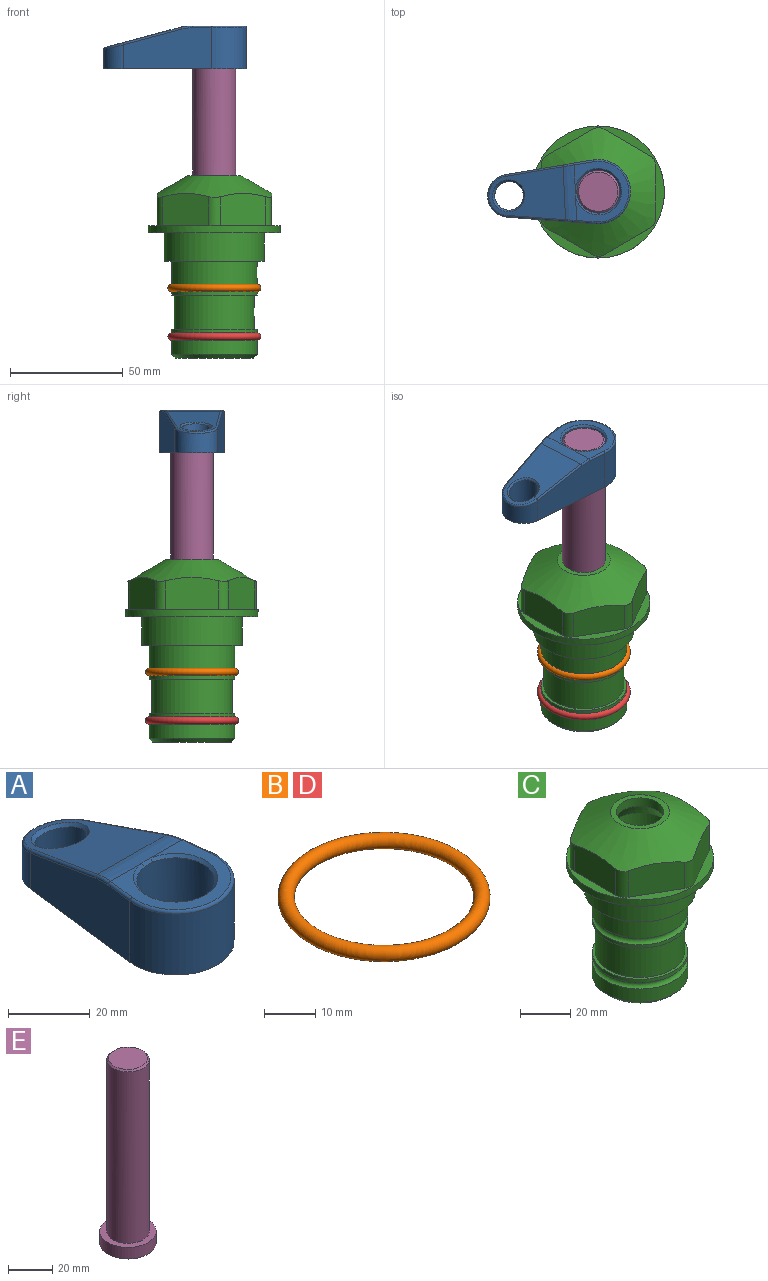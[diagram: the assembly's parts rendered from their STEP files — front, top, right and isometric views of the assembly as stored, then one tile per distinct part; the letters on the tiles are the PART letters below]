
ASSEMBLY  parts=5 mates=4
PART A: 31 faces, bbox 31.7x65.5x19.8 mm
  f0: plane 39.12x18.26mm, normal (0.99,0.12,0), area 612.2mm2, adj f1,f4,f7,f11,f13,f15
  f1: cylinder r=9.53mm len=18.91mm, axis (0,0,-1), area 296.1mm2, adj f0,f2,f7,f17
  f2: plane 39.12x18.26mm, normal (-0.99,0.12,0), area 612.2mm2, adj f1,f4,f7,f12,f14,f16
  f3: cylinder r=6.35mm len=12.7mm, axis (0,0,-1), area 362.4mm2, adj f7,f18
  f4: cylinder r=14.29mm len=28.58mm, axis (0,0,-1), area 882.2mm2, adj f0,f2,f7,f10
  f5: cylinder r=9.53mm len=19.05mm, axis (0,0,-1), area 1092.6mm2, adj f7,f19,f20
  f6: plane 26.99x23.69mm, normal (0,0,1), area 216.2mm2, adj f9,f10,f11,f12,f19
  f7: plane 63.5x28.58mm, normal (0,0,-1), area 661.8mm2, adj f0,f1,f2,f3,f4,f5,f22,f23
  f8: plane 33.52x23.6mm, normal (0,0.26,0.97), area 486mm2, adj f9,f15,f16,f17,f18
  f9: cylinder r=19.05mm len=24.72mm, axis (1,0,0), area 120.4mm2, adj f6,f8,f13,f14,f20
  f10: torus R=13.49mm, axis (0,0,1), area 59mm2, adj f4,f6,f11,f12
  f11: cylinder r=0.79mm len=8.67mm, axis (0.12,-0.99,0), area 10.8mm2, adj f0,f6,f10,f13
  f12: cylinder r=0.79mm len=8.67mm, axis (0.12,0.99,0), area 10.8mm2, adj f2,f6,f10,f14
  f13: bspline ~4.95x1.42mm, area 6.1mm2, adj f0,f9,f11,f15
  f14: bspline ~4.95x1.42mm, area 6.1mm2, adj f2,f9,f12,f16
  f15: cylinder r=0.79mm len=25.95mm, axis (0.12,-0.96,0.26), area 32.9mm2, adj f0,f8,f13,f17
  f16: cylinder r=0.79mm len=25.95mm, axis (0.12,0.96,-0.26), area 32.9mm2, adj f2,f8,f14,f17
  f17: bspline ~18.91x8.38mm, area 30mm2, adj f1,f8,f15,f16
  f18: bspline ~14.29x14.29mm, area 48.3mm2, adj f3,f8
  f19: cone r=9.53mm half-angle=45deg, axis (0,0,1), area 66.5mm2, adj f5,f6,f20
  f20: bspline ~3.22x0.96mm, area 3.5mm2, adj f5,f9,f19
  f21: plane 2.75x2.72mm, normal (0,0,-1), area 2.9mm2, adj f23,f25,f28
  f22: plane 23.05x15.88mm, normal (-0.99,-0.12,0), area 323.6mm2, adj f7,f25,f26,f27,f28,f29
  f23: plane 23.05x15.88mm, normal (0.99,-0.12,0), area 323.6mm2, adj f7,f21,f25,f27,f28,f30
  f24: cylinder r=9.53mm len=10.69mm, axis (0,0,-1), area 114.7mm2, adj f7,f27,f29,f30
  f25: cylinder r=12.7mm len=20.59mm, axis (0,0,-1), area 381.1mm2, adj f7,f21,f22,f23,f26,f28
  f26: plane 2.75x2.72mm, normal (0,0,-1), area 2.9mm2, adj f22,f25,f28
  f27: plane 19.72x18.37mm, normal (0,-0.26,-0.97), area 291.8mm2, adj f22,f23,f24,f28,f29,f30
  f28: cylinder r=15.88mm len=19.92mm, axis (1,0,0), area 54.8mm2, adj f21,f22,f23,f25,f26,f27
  f29: cylinder r=1.59mm len=11mm, axis (0,0,-1), area 34.7mm2, adj f7,f22,f24,f27
  f30: cylinder r=1.59mm len=11mm, axis (0,0,-1), area 34.7mm2, adj f7,f23,f24,f27
PART B: 1 faces, bbox 44.7x44.7x3.2 mm
  f0: torus R=19.05mm, axis (0,0,1), area 1193.9mm2
PART C: 36 faces, bbox 58.7x58.7x81 mm
  f0: cylinder r=17.78mm len=35.56mm, axis (0,0,1), area 1670.8mm2, adj f23,f24,f31
  f1: cylinder r=19.05mm len=38.1mm, axis (0,0,1), area 1191.9mm2, adj f26,f27,f30
  f2: plane 58.66x58.66mm, normal (0,0,-1), area 1150.6mm2, adj f3,f28
  f3: cylinder r=29.33mm len=58.66mm, axis (0,0,-1), area 585.1mm2, adj f2,f4
  f4: plane 58.66x58.66mm, normal (0,0,1), area 475.9mm2, adj f3,f5,f6,f7,f8,f9,f10,f11
  f5: plane 20.32x14.34mm, normal (-0.5,0.87,0), area 324.4mm2, adj f4,f15,f16,f17
  f6: plane 20.32x14.34mm, normal (0.5,0.87,0), area 324.4mm2, adj f4,f14,f15,f17
  f7: plane 23.48x14.34mm, normal (1,0,0), area 324.4mm2, adj f4,f13,f14,f17
  f8: plane 20.32x14.34mm, normal (0.5,-0.87,0), area 324.4mm2, adj f4,f12,f13,f17
  f9: plane 20.32x14.34mm, normal (-0.5,-0.87,0), area 324.4mm2, adj f4,f11,f12,f17
  f10: plane 23.48x14.34mm, normal (-1,0,0), area 324.4mm2, adj f4,f11,f16,f17
  f11: cylinder r=5.08mm len=12.85mm, axis (0,0,-1), area 67.2mm2, adj f4,f9,f10,f17
  f12: cylinder r=5.08mm len=12.85mm, axis (0,0,-1), area 67.2mm2, adj f4,f8,f9,f17
  f13: cylinder r=5.08mm len=12.85mm, axis (0,0,-1), area 67.2mm2, adj f4,f7,f8,f17
  f14: cylinder r=5.08mm len=12.85mm, axis (0,0,-1), area 67.2mm2, adj f4,f6,f7,f17
  f15: cylinder r=5.08mm len=12.85mm, axis (0,0,-1), area 67.2mm2, adj f4,f5,f6,f17
  f16: cylinder r=5.08mm len=12.85mm, axis (0,0,-1), area 67.2mm2, adj f4,f5,f10,f17
  f17: cone r=11.73mm half-angle=60deg, axis (0,0,-1), area 2071.8mm2, adj f5,f6,f7,f8,f9,f10,f11,f12
  f18: plane 23.46x23.46mm, normal (0,0,1), area 147.4mm2, adj f17,f35
  f19: plane 34.93x34.93mm, normal (0,0,-1), area 958mm2, adj f29
  f20: cylinder r=19.05mm len=38.1mm, axis (0,0,1), area 760.1mm2, adj f21,f29
  f21: torus R=19.05mm, axis (0,0,1), area 565.3mm2, adj f20,f22
  f22: cylinder r=19.05mm len=38.1mm, axis (0,0,1), area 190mm2, adj f21,f23
  f23: plane 38.1x38.1mm, normal (0,0,1), area 146.9mm2, adj f0,f22
  f24: plane 38.1x38.1mm, normal (0,0,-1), area 146.9mm2, adj f0,f25
  f25: cylinder r=19.05mm len=38.1mm, axis (0,0,1), area 190mm2, adj f24,f26
  f26: torus R=19.05mm, axis (0,0,1), area 565.3mm2, adj f1,f25
  f27: plane 44.45x44.45mm, normal (0,0,-1), area 411.7mm2, adj f1,f28
  f28: cylinder r=22.23mm len=44.45mm, axis (0,0,1), area 1773.5mm2, adj f2,f27
  f29: cone r=19.05mm half-angle=45deg, axis (0,0,1), area 257.5mm2, adj f19,f20
  f30: cylinder r=3.17mm len=6.75mm, axis (-1,0,0), area 128mm2, adj f1,f33
  f31: cylinder r=3.17mm len=6.35mm, axis (-1,0,0), area 102.5mm2, adj f0,f33
  f32: plane 25.4x25.4mm, normal (0,0,1), area 506.7mm2, adj f33
  f33: cylinder r=12.7mm len=66.42mm, axis (0,0,-1), area 5236.2mm2, adj f30,f31,f32,f34
  f34: cone r=9.53mm half-angle=30deg, axis (0,0,-1), area 443.4mm2, adj f33,f35
  f35: cylinder r=9.53mm len=19.05mm, axis (0,0,-1), area 240.9mm2, adj f18,f34
PART D: same geometry as B
PART E: 6 faces, bbox 25.4x25.4x101.6 mm
  f0: plane 17.46x17.46mm, normal (0,0,1), area 239.5mm2, adj f5
  f1: plane 25.4x25.4mm, normal (0,0,-1), area 506.7mm2, adj f2
  f2: cylinder r=12.7mm len=25.4mm, axis (0,0,1), area 506.7mm2, adj f1,f3
  f3: plane 25.4x25.4mm, normal (0,0,1), area 221.7mm2, adj f2,f4
  f4: cylinder r=9.53mm len=94.46mm, axis (0,0,1), area 5653mm2, adj f3,f5
  f5: cone r=8.73mm half-angle=45deg, axis (0,0,-1), area 64.4mm2, adj f0,f4
PLACE A rot(axis=(0,0,1),92.6deg) t=(0,0,28.35)mm
PLACE B at identity
PLACE C at identity fixed
PLACE D t=(0,0,-21.59)mm
PLACE E rot(axis=(0,0,1),92.6deg) t=(0,0,27.55)mm
MATE fastened B.f0 <-> C.f0  axis (0,0,1) through (0,0,-24.51)mm
MATE fastened E.f2 <-> A.f4  axis (0,0,1) through (0,0,91.05)mm
MATE cylindrical C.f0 <-> E.f2  axis (0,0,1) through (0,0,-50.55)mm
MATE fastened D.f0 <-> C.f0  axis (0,0,1) through (0,0,-46.1)mm
